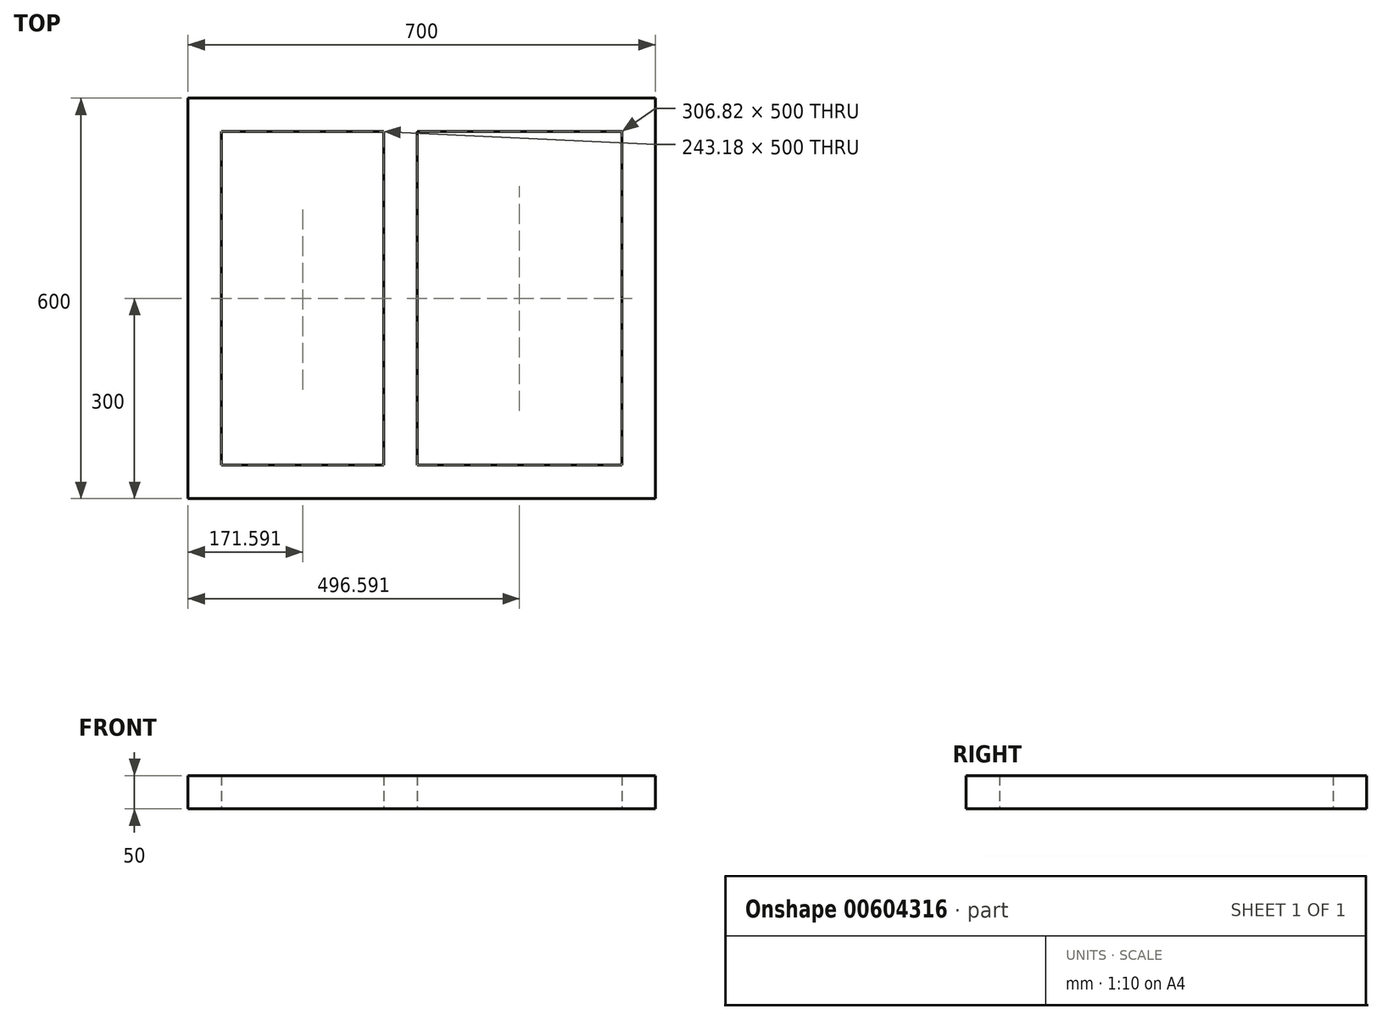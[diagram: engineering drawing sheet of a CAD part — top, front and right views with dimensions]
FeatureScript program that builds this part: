
annotation { "Feature Type Name" : "Feature", "Feature Type Description" : "" }
export const myFeature = defineFeature(function(context is Context, id is Id, definition is map)
    precondition{}
    {
        {
            var Q0;
            Q0=qCreatedBy(makeId("Top.planeOp"),FACE);
            var sketch = newSketch(context, id + "F0", { "sketchPlane" : qUnion([Q0])});
            skLineSegment(sketch, "E0.bottom", {"start": v(350, -300) * mm, "end": v(-350, -300) * mm});
            skLineSegment(sketch, "E0.top", {"start": v(350, 300) * mm, "end": v(-350, 300) * mm});
            skLineSegment(sketch, "E0.left", {"start": v(350, -300) * mm, "end": v(350, 300) * mm});
            skLineSegment(sketch, "E0.right", {"start": v(-350, -300) * mm, "end": v(-350, 300) * mm});
            skPoint(sketch, "E0.middle", {"position": v(0, 0) * mm});
            skLineSegment(sketch, "E1.bottom", {"start": v(300, -250) * mm, "end": v(-300, -250) * mm});
            skLineSegment(sketch, "E1.top", {"start": v(300, 250) * mm, "end": v(-300, 250) * mm});
            skLineSegment(sketch, "E1.left", {"start": v(300, -250) * mm, "end": v(300, 250) * mm});
            skLineSegment(sketch, "E1.right", {"start": v(-300, -250) * mm, "end": v(-300, 250) * mm});
            skSolve(sketch);
        }
        {
            var Q0;
            Q0 = qSketchRegion(id + "F0", true);
            extrude(context, id + "F1", {"entities" : qUnion([Q0]), "depth" : 50 * mm, "offsetDistance" : 25 * mm});
        }
        {
            var Q0;
            Q0=qCreatedBy(makeId("Top.planeOp"),FACE);
            var sketch = newSketch(context, id + "F2", { "sketchPlane" : qUnion([Q0])});
            skLineSegment(sketch, "E2.bottom", {"start": v(-56.82, 250) * mm, "end": v(-6.82, 250) * mm});
            skLineSegment(sketch, "E2.top", {"start": v(-56.82, -250) * mm, "end": v(-6.82, -250) * mm});
            skLineSegment(sketch, "E2.left", {"start": v(-56.82, 250) * mm, "end": v(-56.82, -250) * mm});
            skLineSegment(sketch, "E2.right", {"start": v(-6.82, 250) * mm, "end": v(-6.82, -250) * mm});
            skSolve(sketch);
        }
        {
            var Q0;
            Q0 = qSketchRegion(id + "F2", true);
            extrude(context, id + "F3", {"entities" : qUnion([Q0]), "operationType" : NewBodyOperationType.ADD, "depth" : 50 * mm, "offsetDistance" : 25 * mm});
        }
    });
